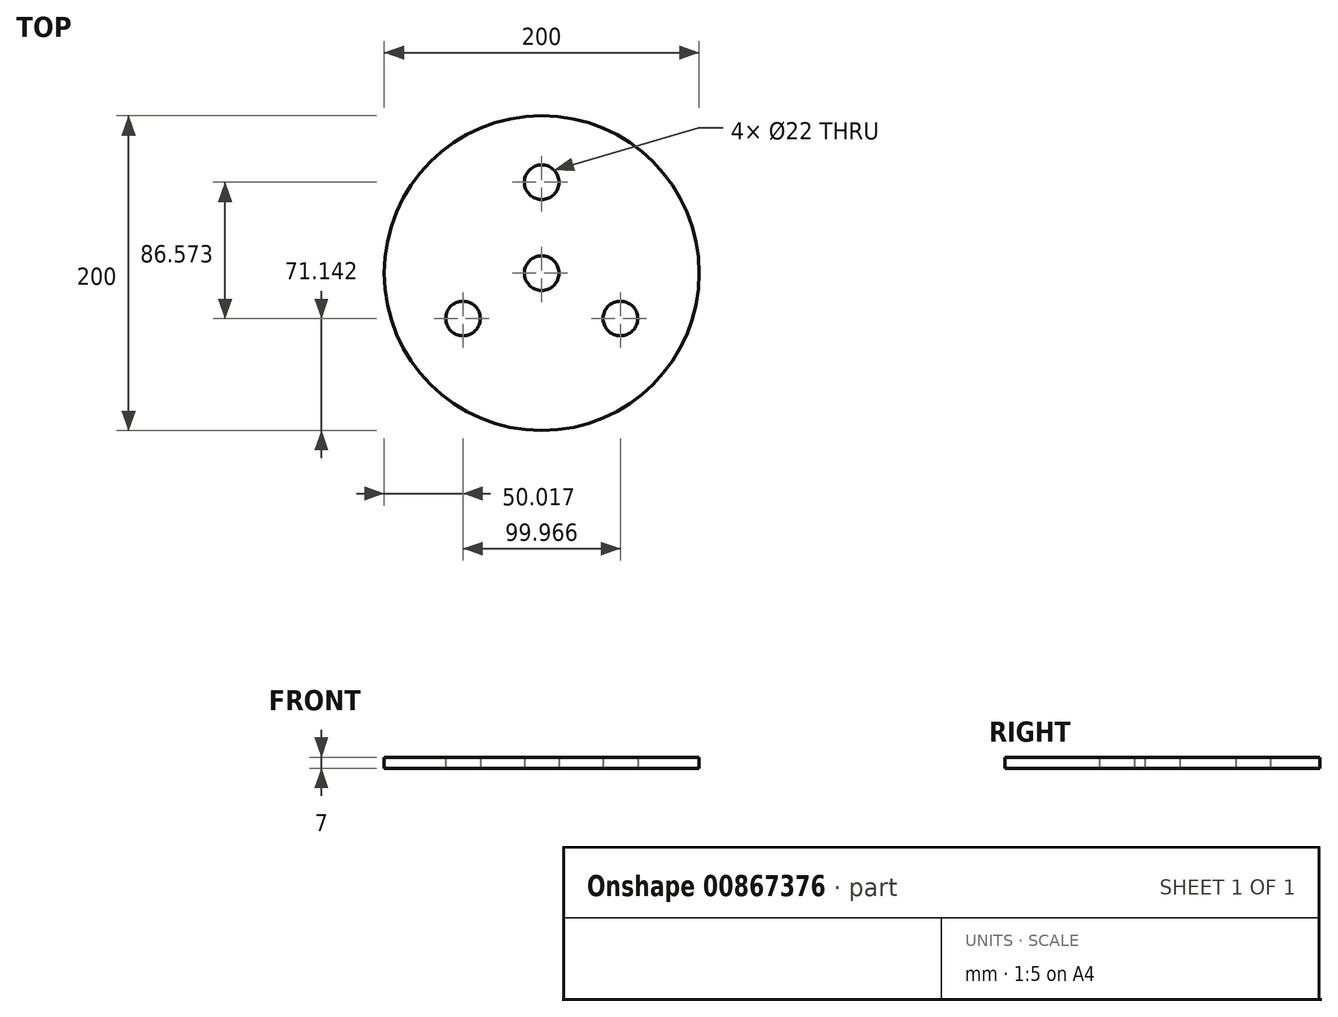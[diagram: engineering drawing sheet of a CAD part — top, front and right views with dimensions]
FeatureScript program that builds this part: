
annotation { "Feature Type Name" : "Feature", "Feature Type Description" : "" }
export const myFeature = defineFeature(function(context is Context, id is Id, definition is map)
    precondition{}
    {
        {
            var Q0;
            Q0=qCreatedBy(makeId("Top.planeOp"),FACE);
            var sketch = newSketch(context, id + "F0", { "sketchPlane" : qUnion([Q0])});
            skCircle(sketch, "E0", {"center": v(0, 0) * mm, "radius": 100 * mm});
            skSolve(sketch);
        }
        {
            var Q0;
            Q0 = qSketchRegion(id + "F0", true);
            extrude(context, id + "F1", {"entities" : qUnion([Q0]), "depth" : 7 * mm, "offsetDistance" : 25.4 * mm});
        }
        {
            var Q0;
            Q0=qCreatedBy(makeId("Top.planeOp"),FACE);
            var sketch = newSketch(context, id + "F2", { "sketchPlane" : qUnion([Q0])});
            skCircle(sketch, "E1", {"center": v(0, 0) * mm, "radius": 11 * mm});
            skCircle(sketch, "E2", {"center": v(0, 57.72) * mm, "radius": 11 * mm});
            skCircle(sketch, "E3.1.0", {"center": v(-49.98, -28.86) * mm, "radius": 11 * mm});
            skCircle(sketch, "E3.2.0", {"center": v(49.98, -28.86) * mm, "radius": 11 * mm});
            skSolve(sketch);
        }
        {
            var Q0;
            Q0 = qSketchRegion(id + "F2", true);
            extrude(context, id + "F3", {"entities" : qUnion([Q0]), "operationType" : NewBodyOperationType.REMOVE, "depth" : 25 * mm, "offsetDistance" : 25 * mm});
        }
    });
